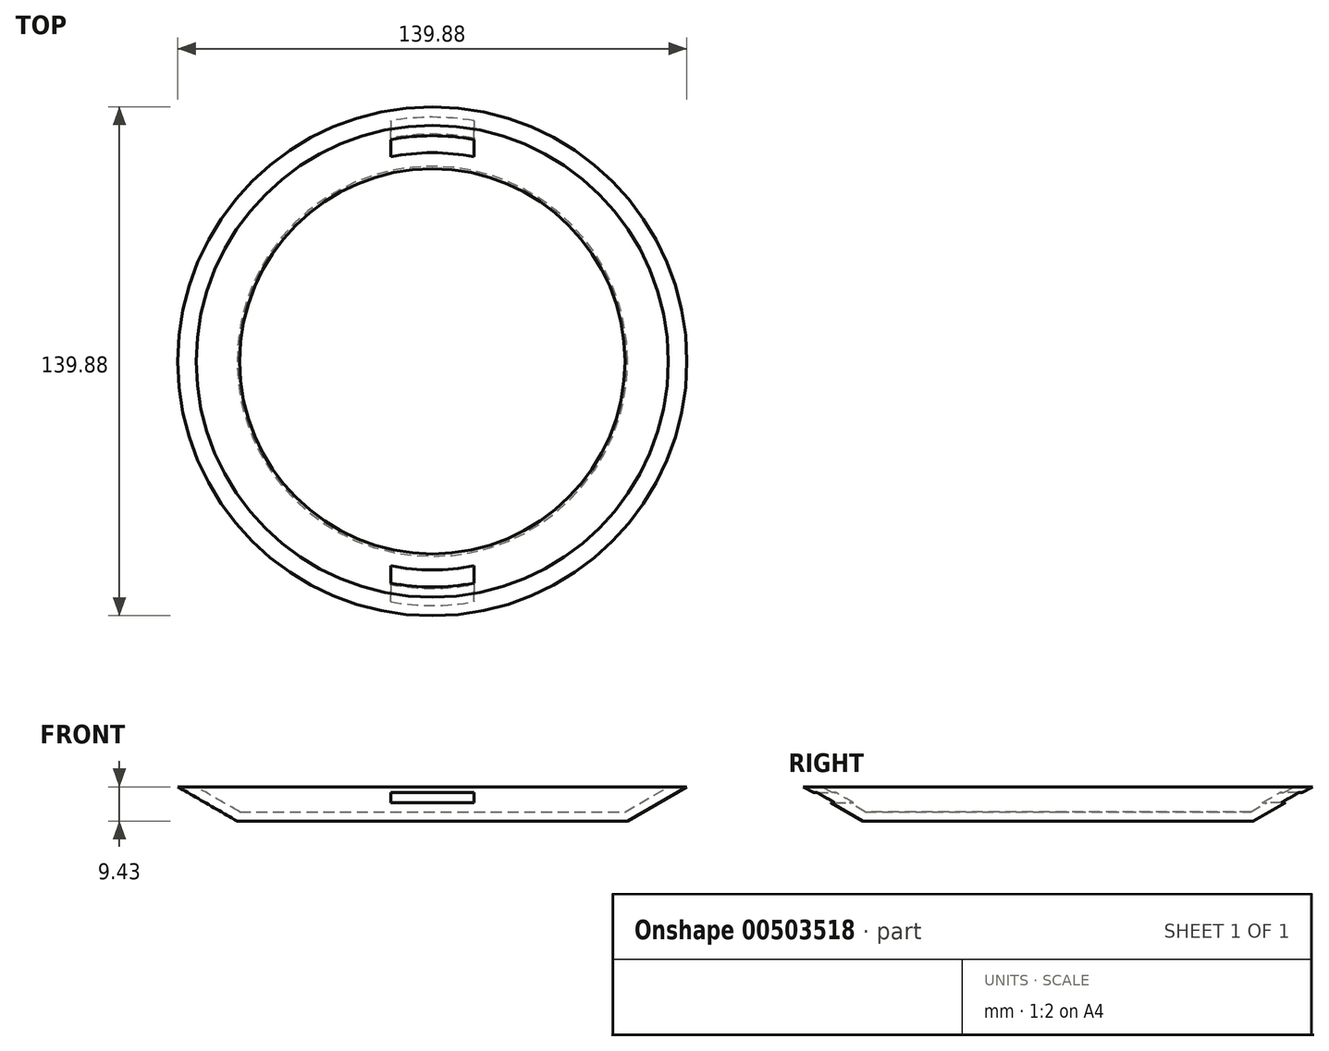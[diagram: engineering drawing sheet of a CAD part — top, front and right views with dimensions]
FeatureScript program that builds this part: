
annotation { "Feature Type Name" : "Feature", "Feature Type Description" : "" }
export const myFeature = defineFeature(function(context is Context, id is Id, definition is map)
    precondition{}
    {
        {
            var Q0;
            Q0=qCreatedBy(makeId("Front.planeOp"),FACE);
            var sketch = newSketch(context, id + "F0", { "sketchPlane" : qUnion([Q0])});
            skLineSegment(sketch, "E0", {"start": v(-53.61, 0) * mm, "end": v(53.61, 0) * mm});
            skLineSegment(sketch, "E1", {"start": v(-53.61, 0) * mm, "end": v(-69.94, 9.43) * mm});
            skLineSegment(sketch, "E2", {"start": v(-69.94, 9.43) * mm, "end": v(69.94, 9.43) * mm});
            skLineSegment(sketch, "E3", {"start": v(69.94, 9.43) * mm, "end": v(53.61, 0) * mm});
            skLineSegment(sketch, "E4", {"start": v(0, 0) * mm, "end": v(0, 9.43) * mm});
            skSolve(sketch);
        }
        {
            var Q0;
            {var subQ0=sQuery(id+"F0.wireOp",EDGE,"E3");Q0=makeQuery(id+"F0.imprint","IMPRINT",FACE,{"disambiguationData":[TD([[makeQuery(id+"F0.imprint","IMPRINT",EDGE,{"derivedFrom":subQ0}),-1.0]])]});}
            var Q1;
            Q1=sQuery(id+"F0.wireOp",EDGE,"E4");
            revolve(context, id + "F1", {"entities" : qUnion([Q0]), "axis" : qUnion([Q1]), "revolveType" : RevolveType.FULL});
        }
        {
            var Q0;
            Q0=makeQuery(id+"F1.opRevolve","SWEPT_FACE",FACE,{"disambiguationData":[OSD([sQuery(id+"F0.wireOp",EDGE,"E2")])]});
            shell(context, id + "F2", {"entities" : qUnion([Q0]), "thickness" : 2.54 * mm});
        }
        {
            var Q0;
            Q0=qCreatedBy(makeId("Front.planeOp"),FACE);
            var sketch = newSketch(context, id + "F3", { "sketchPlane" : qUnion([Q0])});
            skLineSegment(sketch, "E5.bottom", {"start": v(11.44, 5.08) * mm, "end": v(-11.44, 5.08) * mm});
            skLineSegment(sketch, "E5.top", {"start": v(11.44, 7.78) * mm, "end": v(-11.44, 7.78) * mm});
            skLineSegment(sketch, "E5.left", {"start": v(11.44, 5.08) * mm, "end": v(11.44, 7.78) * mm});
            skLineSegment(sketch, "E5.right", {"start": v(-11.44, 5.08) * mm, "end": v(-11.44, 7.78) * mm});
            skPoint(sketch, "E5.middle", {"position": v(0, 6.43) * mm});
            skSolve(sketch);
        }
        {
            var Q0;
            Q0 = qSketchRegion(id + "F3", true);
            extrude(context, id + "F4", {"entities" : qUnion([Q0]), "operationType" : NewBodyOperationType.REMOVE, "endBound" : BoundingType.THROUGH_ALL, "oppositeDirection" : true, "depth" : 25.4 * mm});
        }
        {
            var Q0;
            Q0=makeQuery(id+"F3.imprint","IMPRINT",FACE,{"disambiguationData":[TD([[makeQuery(id+"F3.imprint","IMPRINT",EDGE,{"derivedFrom":sQuery(id+"F3.wireOp",EDGE,"E5.bottom")}),-1.0]])]});
            extrude(context, id + "F5", {"entities" : qUnion([Q0]), "operationType" : NewBodyOperationType.REMOVE, "endBound" : BoundingType.THROUGH_ALL, "depth" : 25.4 * mm});
        }
    });
